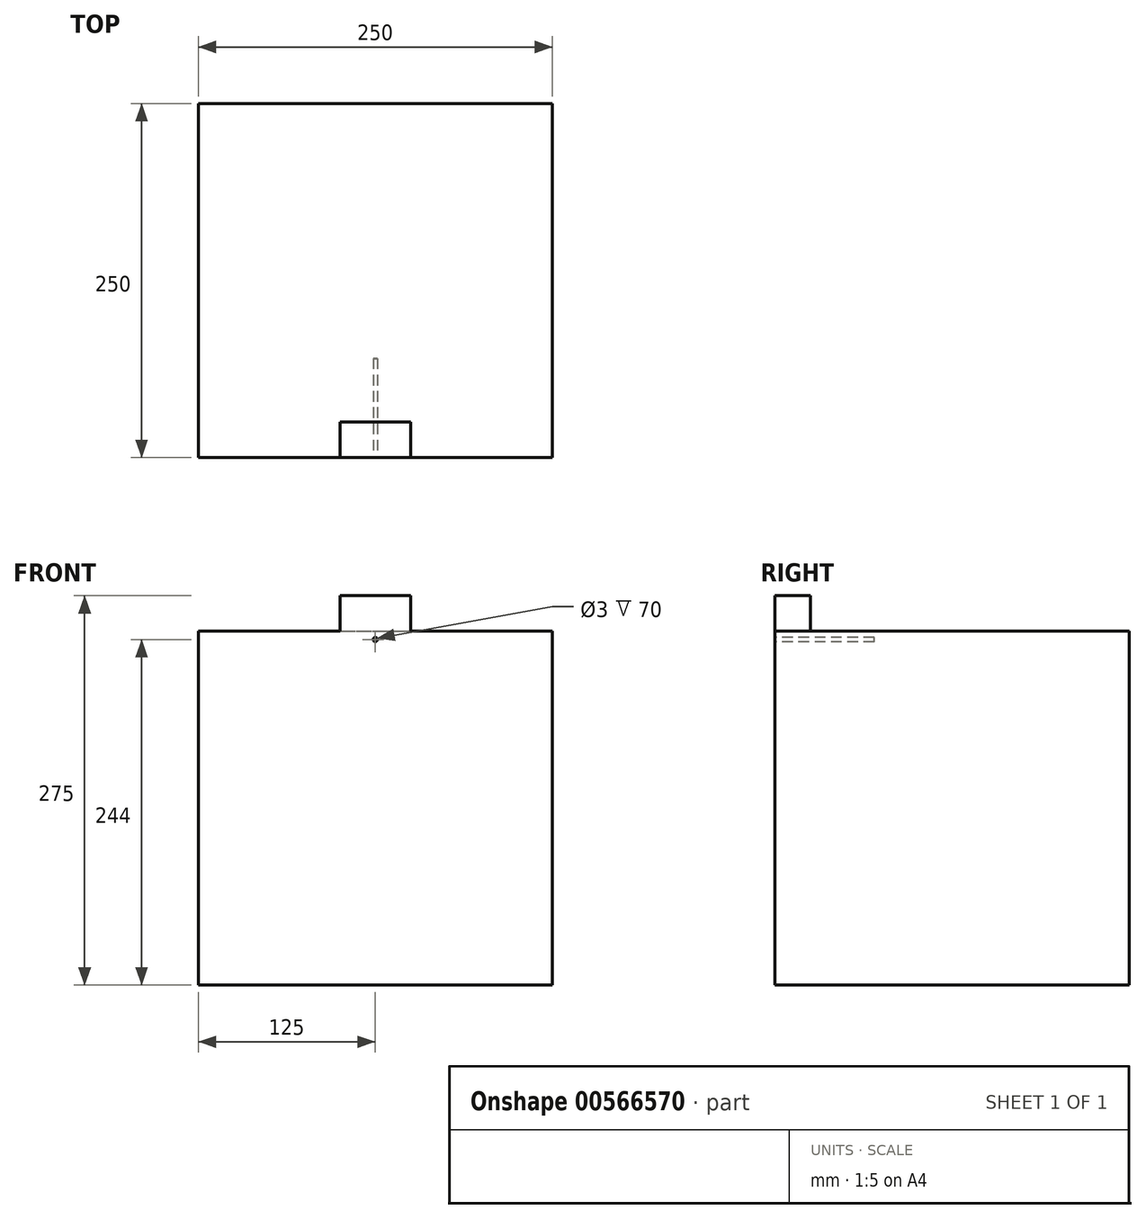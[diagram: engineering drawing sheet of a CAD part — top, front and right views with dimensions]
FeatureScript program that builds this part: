
annotation { "Feature Type Name" : "Feature", "Feature Type Description" : "" }
export const myFeature = defineFeature(function(context is Context, id is Id, definition is map)
    precondition{}
    {
        {
            var Q0;
            Q0=qCreatedBy(makeId("Top.planeOp"),FACE);
            var sketch = newSketch(context, id + "F0", { "sketchPlane" : qUnion([Q0])});
            skLineSegment(sketch, "E0.bottom", {"start": v(-62.45, 204.72) * mm, "end": v(187.55, 204.72) * mm});
            skLineSegment(sketch, "E0.top", {"start": v(-62.45, -45.28) * mm, "end": v(187.55, -45.28) * mm});
            skLineSegment(sketch, "E0.left", {"start": v(-62.45, 204.72) * mm, "end": v(-62.45, -45.28) * mm});
            skLineSegment(sketch, "E0.right", {"start": v(187.55, 204.72) * mm, "end": v(187.55, -45.28) * mm});
            skSolve(sketch);
        }
        {
            var Q0;
            Q0 = qSketchRegion(id + "F0", true);
            extrude(context, id + "F1", {"entities" : qUnion([Q0]), "depth" : 250 * mm, "offsetDistance" : 25 * mm});
        }
        {
            var Q0;
            Q0=makeQuery(id+"F1.opExtrude","CAP_FACE",FACE,{"disambiguationData":[OSD([sQuery(id+"F0.wireOp",EDGE,"E0.bottom"),sQuery(id+"F0.wireOp",EDGE,"E0.top"),sQuery(id+"F0.wireOp",EDGE,"E0.left"),sQuery(id+"F0.wireOp",EDGE,"E0.right")])],"isStart":false});
            var sketch = newSketch(context, id + "F2", { "sketchPlane" : qUnion([Q0])});
            skLineSegment(sketch, "E1", {"start": v(-62.45, 51.05) * mm, "end": v(187.55, 51.05) * mm, "construction": true});
            skLineSegment(sketch, "E2", {"start": v(62.55, 51.05) * mm, "end": v(62.55, -45.28) * mm, "construction": true});
            skLineSegment(sketch, "E3", {"start": v(62.55, -45.28) * mm, "end": v(37.55, -45.28) * mm});
            skLineSegment(sketch, "E4", {"start": v(62.55, -45.28) * mm, "end": v(87.55, -45.28) * mm});
            skLineSegment(sketch, "E5", {"start": v(37.55, -45.28) * mm, "end": v(37.55, -20.28) * mm});
            skLineSegment(sketch, "E6", {"start": v(37.55, -20.28) * mm, "end": v(87.55, -20.28) * mm});
            skLineSegment(sketch, "E7", {"start": v(87.55, -20.28) * mm, "end": v(87.55, -45.28) * mm});
            skSolve(sketch);
        }
        {
            var Q0;
            Q0 = qSketchRegion(id + "F2", true);
            extrude(context, id + "F3", {"entities" : qUnion([Q0]), "operationType" : NewBodyOperationType.ADD, "depth" : 25 * mm, "offsetDistance" : 25 * mm});
        }
        {
            var Q0;
            Q0=makeQuery(id+"F3.boolean.opBoolean","MERGE",FACE,{"derivedFrom":[makeQuery(id+"F1.opExtrude","SWEPT_FACE",FACE,{"disambiguationData":[OSD([sQuery(id+"F0.wireOp",EDGE,"E0.top")])]}),makeQuery(id+"F3.opExtrude","SWEPT_FACE",FACE,{"disambiguationData":[OSD([sQuery(id+"F2.wireOp",EDGE,"E3"),sQuery(id+"F2.wireOp",EDGE,"E4")])]})]});
            var sketch = newSketch(context, id + "F4", { "sketchPlane" : qUnion([Q0])});
            skLineSegment(sketch, "E8", {"start": v(37.55, 250) * mm, "end": v(87.55, 250) * mm, "construction": true});
            skLineSegment(sketch, "E9", {"start": v(62.55, 250) * mm, "end": v(62.55, 244) * mm, "construction": true});
            skCircle(sketch, "E10", {"center": v(62.55, 244) * mm, "radius": 1.5 * mm});
            skSolve(sketch);
        }
        {
            var Q0;
            Q0 = qSketchRegion(id + "F4", true);
            extrude(context, id + "F5", {"entities" : qUnion([Q0]), "operationType" : NewBodyOperationType.REMOVE, "oppositeDirection" : true, "depth" : 70 * mm, "offsetDistance" : 25 * mm});
        }
    });
